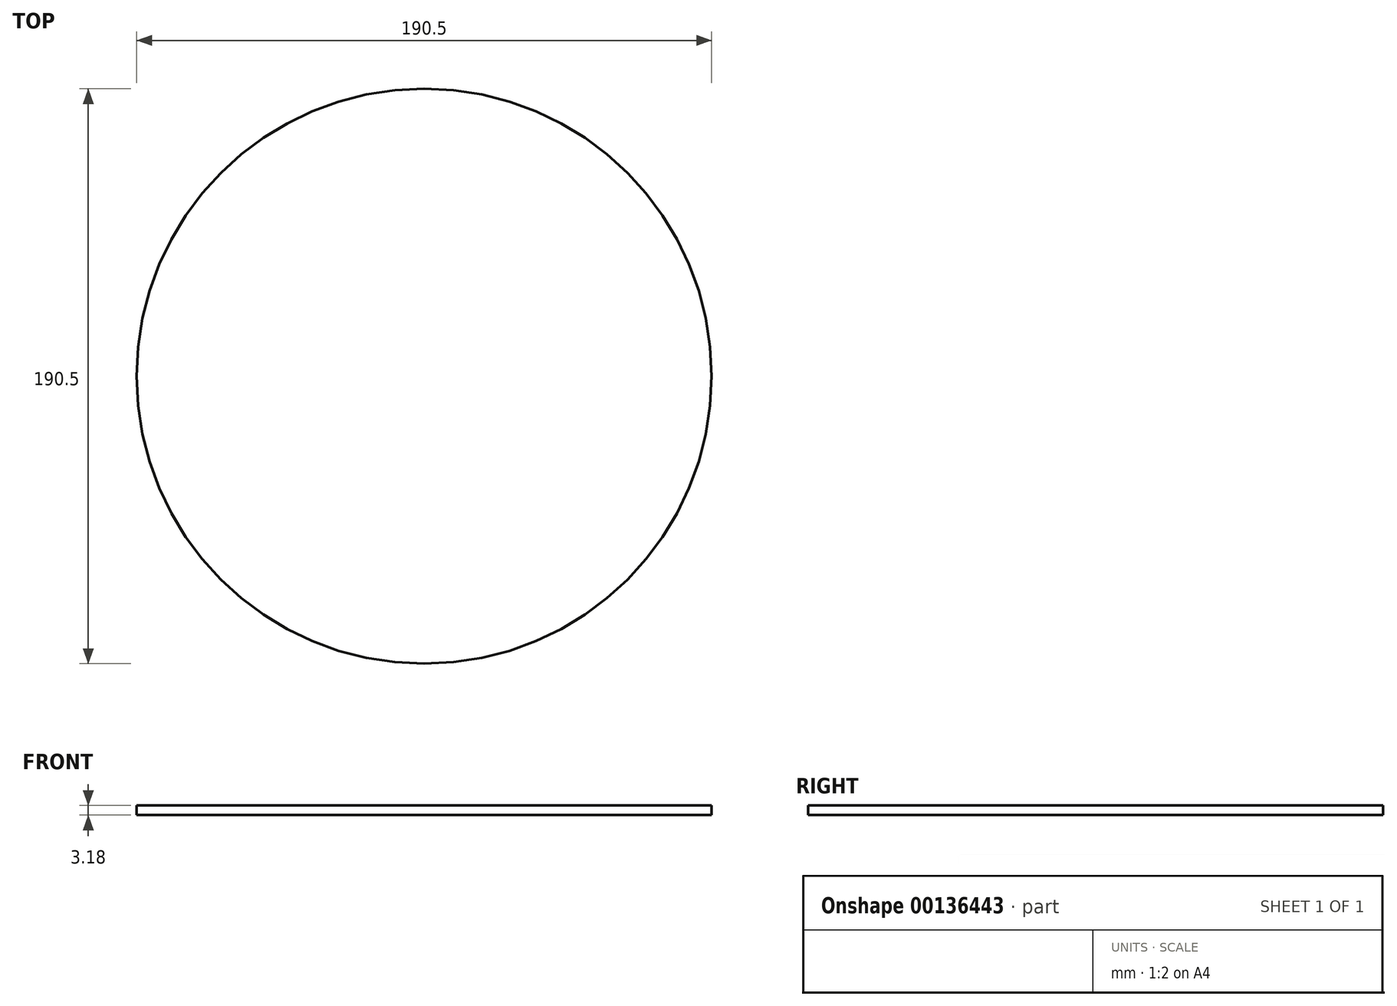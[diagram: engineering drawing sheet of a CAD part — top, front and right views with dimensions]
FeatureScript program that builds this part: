
annotation { "Feature Type Name" : "Feature", "Feature Type Description" : "" }
export const myFeature = defineFeature(function(context is Context, id is Id, definition is map)
    precondition{}
    {
        {
            var Q0;
            Q0=qCreatedBy(makeId("Top.planeOp"),FACE);
            var sketch = newSketch(context, id + "F0", { "sketchPlane" : qUnion([Q0])});
            skCircle(sketch, "E0", {"center": v(0, 0) * mm, "radius": 95.25 * mm});
            skSolve(sketch);
        }
        {
            var Q0;
            Q0 = qSketchRegion(id + "F0", true);
            extrude(context, id + "F1", {"entities" : qUnion([Q0]), "depth" : 3.17 * mm});
        }
    });
